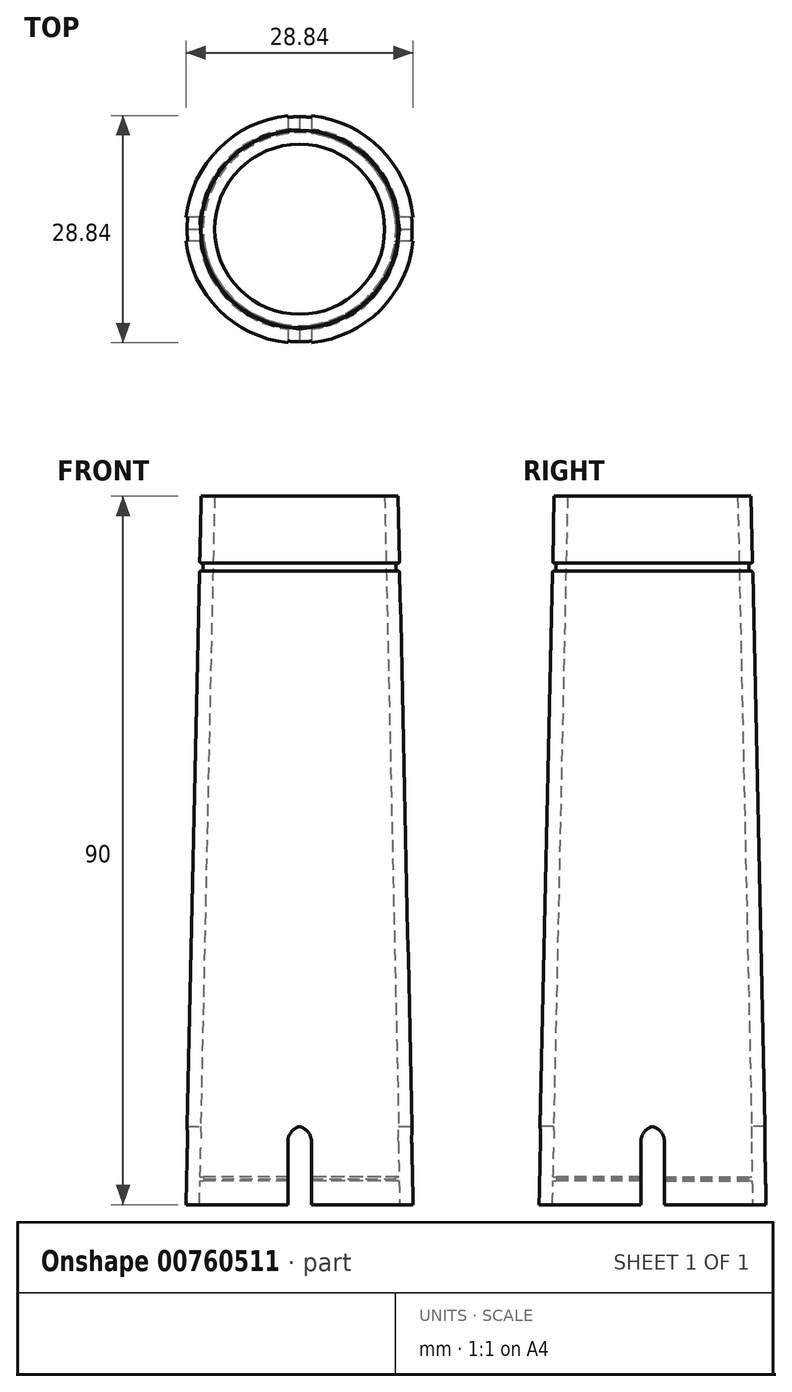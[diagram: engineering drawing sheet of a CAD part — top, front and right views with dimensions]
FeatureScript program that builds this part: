
annotation { "Feature Type Name" : "Feature", "Feature Type Description" : "" }
export const myFeature = defineFeature(function(context is Context, id is Id, definition is map)
    precondition{}
    {
        {
            var Q0;
            Q0=qCreatedBy(makeId("Top.planeOp"),FACE);
            var sketch = newSketch(context, id + "F0", { "sketchPlane" : qUnion([Q0])});
            skCircle(sketch, "E0", {"center": v(0, 0) * mm, "radius": 14.5 * mm});
            skCircle(sketch, "E1", {"center": v(0, 0) * mm, "radius": 12.8 * mm, "construction": true});
            skLineSegment(sketch, "E2", {"start": v(0, 14.5) * mm, "end": v(0, -14.5) * mm, "construction": true});
            skLineSegment(sketch, "E3", {"start": v(-14.5, 0) * mm, "end": v(14.5, 0) * mm, "construction": true});
            skSolve(sketch);
        }
        {
            var Q0;
            Q0=qCreatedBy(makeId("Top.planeOp"),FACE);
            cPlane(context, id + "F1", {"entities" : qUnion([Q0]), "cplaneType" : CPlaneType.OFFSET, "offset" : 90 * mm, "width" : 150 * mm, "height" : 150 * mm});
        }
        {
            var Q0;
            Q0=qCreatedBy(id+"F1.planeOp",FACE);
            var sketch = newSketch(context, id + "F2", { "sketchPlane" : qUnion([Q0])});
            skCircle(sketch, "E4", {"center": v(0, 0) * mm, "radius": 12.5 * mm});
            skCircle(sketch, "E5", {"center": v(0, 0) * mm, "radius": 10.8 * mm, "construction": true});
            skSolve(sketch);
        }
        {
            var Q0;
            Q0=makeQuery(id+"F0.imprint","IMPRINT",FACE,{"disambiguationData":[TD([[makeQuery(id+"F0.imprint","IMPRINT",EDGE,{"derivedFrom":sQuery(id+"F0.wireOp",EDGE,"E0")}),1.0]])]});
            var Q1;
            Q1=makeQuery(id+"F2.imprint","IMPRINT",FACE,{"disambiguationData":[TD([[makeQuery(id+"F2.imprint","IMPRINT",EDGE,{"derivedFrom":sQuery(id+"F2.wireOp",EDGE,"E4")}),1.0]])]});
            var Q2;
            Q2=sQuery(id+"F2.wireOp",EDGE,"E4");
            var Q3;
            Q3=sQuery(id+"F0.wireOp",EDGE,"E0");
            loft(context, id + "F3", {"sheetProfilesArray" : [{ "sheetProfileEntities" : qUnion([Q0]) }, { "sheetProfileEntities" : qUnion([Q1]) }], "wireProfilesArray" : [{ "wireProfileEntities" : qUnion([Q2]) }, { "wireProfileEntities" : qUnion([Q3]) }]});
        }
        {
            var Q0;
            Q0=qCreatedBy(makeId("Top.planeOp"),FACE);
            var sketch = newSketch(context, id + "F4", { "sketchPlane" : qUnion([Q0])});
            skCircle(sketch, "E6", {"center": v(0, 0) * mm, "radius": 14.5 * mm, "construction": true});
            skCircle(sketch, "E7", {"center": v(0, 0) * mm, "radius": 12.8 * mm});
            skSolve(sketch);
        }
        {
            var Q0;
            Q0=makeQuery(id+"F2.imprint","IMPRINT",FACE,{"disambiguationData":[TD([[makeQuery(id+"F2.imprint","IMPRINT",EDGE,{"derivedFrom":sQuery(id+"F2.wireOp",EDGE,"E4")}),1.0]])]});
            var sketch = newSketch(context, id + "F5", { "sketchPlane" : qUnion([Q0])});
            skCircle(sketch, "E8", {"center": v(0, 0) * mm, "radius": 10.8 * mm});
            skSolve(sketch);
        }
        {
            var Q1;
            Q1=makeQuery(id+"F5.imprint","IMPRINT",FACE,{"disambiguationData":[TD([[makeQuery(id+"F5.imprint","IMPRINT",EDGE,{"derivedFrom":sQuery(id+"F5.wireOp",EDGE,"E8")}),1.0]])]});
            var Q2;
            Q2=makeQuery(id+"F4.imprint","IMPRINT",FACE,{"disambiguationData":[TD([[makeQuery(id+"F4.imprint","IMPRINT",EDGE,{"derivedFrom":sQuery(id+"F4.wireOp",EDGE,"E7")}),1.0]])]});
            loft(context, id + "F6", {"operationType" : NewBodyOperationType.REMOVE, "sheetProfilesArray" : [{ "sheetProfileEntities" : qUnion([Q1]) }, { "sheetProfileEntities" : qUnion([Q2]) }]});
        }
        {
            var Q0;
            Q0=qCreatedBy(makeId("Top.planeOp"),FACE);
            cPlane(context, id + "F7", {"entities" : qUnion([Q0]), "cplaneType" : CPlaneType.OFFSET, "offset" : 81 * mm, "width" : 150 * mm, "height" : 150 * mm});
        }
        {
            var Q0;
            Q0=qCreatedBy(id+"F7.planeOp",FACE);
            var sketch = newSketch(context, id + "F8", { "sketchPlane" : qUnion([Q0])});
            skCircle(sketch, "E9", {"center": v(0, 0) * mm, "radius": 12.25 * mm});
            skCircle(sketch, "E10", {"center": v(0, 0) * mm, "radius": 14.5 * mm});
            skSolve(sketch);
        }
        {
            var Q0;
            Q0=makeQuery(id+"F8.imprint","IMPRINT",FACE,{"disambiguationData":[TD([[makeQuery(id+"F8.imprint","IMPRINT",EDGE,{"derivedFrom":sQuery(id+"F8.wireOp",EDGE,"E9")}),-1.0]])]});
            extrude(context, id + "F9", {"entities" : qUnion([Q0]), "operationType" : NewBodyOperationType.REMOVE, "depth" : 0.5 * mm, "offsetDistance" : 25 * mm});
        }
        {
            var Q0;
            Q0 = qSketchRegion(id + "F8", true);
            extrude(context, id + "F10", {"entities" : qUnion([Q0]), "operationType" : NewBodyOperationType.REMOVE, "oppositeDirection" : true, "depth" : 0.5 * mm, "offsetDistance" : 25 * mm});
        }
        {
            var Q0;
            Q0=makeQuery(id+"F9.boolean.opBoolean","INTERSECT",EDGE,{"derivedFrom":[makeQuery(id+"F3.opLoft","SWEPT_FACE",FACE,{"disambiguationData":[OSD([sQuery(id+"F0.wireOp",EDGE,"E0"),sQuery(id+"F2.wireOp",EDGE,"E4")])]}),makeQuery(id+"F9.opExtrude","CAP_FACE",FACE,{"disambiguationData":[OSD([sQuery(id+"F8.wireOp",EDGE,"E9"),sQuery(id+"F8.wireOp",EDGE,"E10")])],"isStart":false})]});
            var Q1;
            {var subQ0=sQuery(id+"F8.wireOp",EDGE,"E10");var subQ1=sQuery(id+"F8.wireOp",EDGE,"E9");var subQ2=sQuery(id+"F0.wireOp",EDGE,"E0");Q1=makeQuery(id+"F10.boolean.opBoolean","INTERSECT",EDGE,{"derivedFrom":[makeQuery(id+"F9.boolean.opBoolean","SPLIT",FACE,{"disambiguationData":[TD([makeQuery(id+"F3.opLoft","CAP_FACE",FACE,{"disambiguationData":[OSD([makeQuery(id+"F0.imprint","IMPRINT",FACE,{"disambiguationData":[TD([[makeQuery(id+"F0.imprint","IMPRINT",EDGE,{"derivedFrom":subQ2}),1.0]])]})])],"isStart":true})])],"derivedFrom":makeQuery(id+"F3.opLoft","SWEPT_FACE",FACE,{"disambiguationData":[OSD([subQ2,sQuery(id+"F2.wireOp",EDGE,"E4")])]})}),makeQuery(id+"F10.opExtrude","CAP_FACE",FACE,{"disambiguationData":[OSD([subQ1,subQ0])],"isStart":false})]});}
            fillet(context, id + "F11", {"entities" : qUnion([Q0, Q1]), "radius" : 0.2 * mm, "tangentPropagation" : true, "allowEdgeOverflow" : false});
        }
        {
            var Q0;
            Q0=qCreatedBy(makeId("Top.planeOp"),FACE);
            cPlane(context, id + "F12", {"entities" : qUnion([Q0]), "cplaneType" : CPlaneType.OFFSET, "offset" : 3 * mm, "width" : 150 * mm, "height" : 150 * mm});
        }
        {
            var Q0;
            Q0=qCreatedBy(id+"F12.planeOp",FACE);
            var sketch = newSketch(context, id + "F13", { "sketchPlane" : qUnion([Q0])});
            skCircle(sketch, "E11", {"center": v(0, 0) * mm, "radius": 14 * mm});
            skCircle(sketch, "E12", {"center": v(0, 0) * mm, "radius": 12.2 * mm});
            skSolve(sketch);
        }
        {
            var Q0;
            Q0 = qSketchRegion(id + "F13", true);
            extrude(context, id + "F14", {"entities" : qUnion([Q0]), "operationType" : NewBodyOperationType.ADD, "depth" : 0.5 * mm, "offsetDistance" : 25 * mm});
        }
        {
            var Q0;
            Q0 = qSketchRegion(id + "F13", true);
            extrude(context, id + "F15", {"entities" : qUnion([Q0]), "operationType" : NewBodyOperationType.ADD, "depth" : 0.5 * mm, "offsetDistance" : 25 * mm});
        }
        {
            var Q0;
            Q0=makeQuery(id+"F0.imprint","IMPRINT",FACE,{"disambiguationData":[TD([[makeQuery(id+"F0.imprint","IMPRINT",EDGE,{"derivedFrom":sQuery(id+"F0.wireOp",EDGE,"E0")}),1.0]])]});
            var sketch = newSketch(context, id + "F16", { "sketchPlane" : qUnion([Q0])});
            skLineSegment(sketch, "E13.bottom", {"start": v(-1.5, 16.5) * mm, "end": v(1.5, 16.5) * mm});
            skLineSegment(sketch, "E13.top", {"start": v(-1.5, -16.5) * mm, "end": v(1.5, -16.5) * mm});
            skLineSegment(sketch, "E13.left", {"start": v(-1.5, 16.5) * mm, "end": v(-1.5, -16.5) * mm});
            skLineSegment(sketch, "E13.right", {"start": v(1.5, 16.5) * mm, "end": v(1.5, -16.5) * mm});
            skPoint(sketch, "E13.middle", {"position": v(0, 0) * mm});
            skLineSegment(sketch, "E14.bottom", {"start": v(16.5, 1.5) * mm, "end": v(-16.5, 1.5) * mm});
            skLineSegment(sketch, "E14.top", {"start": v(16.5, -1.5) * mm, "end": v(-16.5, -1.5) * mm});
            skLineSegment(sketch, "E14.left", {"start": v(16.5, 1.5) * mm, "end": v(16.5, -1.5) * mm});
            skLineSegment(sketch, "E14.right", {"start": v(-16.5, 1.5) * mm, "end": v(-16.5, -1.5) * mm});
            skSolve(sketch);
        }
        {
            var Q0;
            Q0 = qSketchRegion(id + "F16", true);
            extrude(context, id + "F17", {"entities" : qUnion([Q0]), "operationType" : NewBodyOperationType.REMOVE, "depth" : 10 * mm, "offsetDistance" : 25 * mm});
        }
        {
            var Q0;
            {var subQ0=sQuery(id+"F13.wireOp",EDGE,"E12");var subQ1=sQuery(id+"F16.wireOp",EDGE,"E13.left");var subQ4=sQuery(id+"F16.wireOp",EDGE,"E14.top");var subQ5=makeQuery(id+"F16.imprint","INTERSECT",VERTEX,{"derivedFrom":[subQ1,subQ4]});Q0=makeQuery(id+"F17.boolean.opBoolean","SPLIT",EDGE,{"disambiguationData":[TD([makeQuery(id+"F17.opExtrude","SWEPT_FACE",FACE,{"disambiguationData":[OSD([subQ1]),TDD([makeQuery(id+"F16.imprint","IMPRINT",EDGE,{"disambiguationData":[TD([[subQ5,-1.0]])],"derivedFrom":subQ1}),makeQuery(id+"F16.imprint","IMPRINT",EDGE,{"disambiguationData":[TD([[makeQuery(id+"F16.imprint","INTERSECT",VERTEX,{"derivedFrom":[sQuery(id+"F16.wireOp",EDGE,"E13.top"),subQ1]}),1.0]])],"derivedFrom":subQ1})])]})])],"derivedFrom":makeQuery(id+"F14.opExtrude","CAP_EDGE",EDGE,{"disambiguationData":[OSD([subQ0])],"isStart":true})});}
            var Q1;
            {var subQ0=sQuery(id+"F13.wireOp",EDGE,"E12");var subQ1=sQuery(id+"F16.wireOp",EDGE,"E13.left");var subQ4=sQuery(id+"F16.wireOp",EDGE,"E14.top");var subQ5=makeQuery(id+"F16.imprint","INTERSECT",VERTEX,{"derivedFrom":[subQ1,subQ4]});Q1=makeQuery(id+"F17.boolean.opBoolean","SPLIT",EDGE,{"disambiguationData":[TD([makeQuery(id+"F17.opExtrude","SWEPT_FACE",FACE,{"disambiguationData":[OSD([subQ1]),TDD([makeQuery(id+"F16.imprint","IMPRINT",EDGE,{"disambiguationData":[TD([[subQ5,-1.0]])],"derivedFrom":subQ1}),makeQuery(id+"F16.imprint","IMPRINT",EDGE,{"disambiguationData":[TD([[makeQuery(id+"F16.imprint","INTERSECT",VERTEX,{"derivedFrom":[sQuery(id+"F16.wireOp",EDGE,"E13.top"),subQ1]}),1.0]])],"derivedFrom":subQ1})])]})])],"derivedFrom":makeQuery(id+"F14.opExtrude","CAP_EDGE",EDGE,{"disambiguationData":[OSD([subQ0])],"isStart":false})});}
            var Q2;
            {var subQ0=sQuery(id+"F13.wireOp",EDGE,"E12");var subQ1=sQuery(id+"F16.wireOp",EDGE,"E14.top");var subQ2=sQuery(id+"F16.wireOp",EDGE,"E13.right");var subQ3=makeQuery(id+"F16.imprint","INTERSECT",VERTEX,{"derivedFrom":[subQ2,subQ1]});Q2=makeQuery(id+"F17.boolean.opBoolean","SPLIT",EDGE,{"disambiguationData":[TD([makeQuery(id+"F17.opExtrude","SWEPT_FACE",FACE,{"disambiguationData":[OSD([subQ2]),TDD([makeQuery(id+"F16.imprint","IMPRINT",EDGE,{"disambiguationData":[TD([[subQ3,-1.0]])],"derivedFrom":subQ2}),makeQuery(id+"F16.imprint","IMPRINT",EDGE,{"disambiguationData":[TD([[makeQuery(id+"F16.imprint","INTERSECT",VERTEX,{"derivedFrom":[sQuery(id+"F16.wireOp",EDGE,"E13.top"),subQ2]}),1.0]])],"derivedFrom":subQ2})])]})])],"derivedFrom":makeQuery(id+"F14.opExtrude","CAP_EDGE",EDGE,{"disambiguationData":[OSD([subQ0])],"isStart":true})});}
            var Q3;
            {var subQ0=sQuery(id+"F13.wireOp",EDGE,"E12");var subQ1=sQuery(id+"F16.wireOp",EDGE,"E14.top");var subQ2=sQuery(id+"F16.wireOp",EDGE,"E13.right");var subQ3=makeQuery(id+"F16.imprint","INTERSECT",VERTEX,{"derivedFrom":[subQ2,subQ1]});Q3=makeQuery(id+"F17.boolean.opBoolean","SPLIT",EDGE,{"disambiguationData":[TD([makeQuery(id+"F17.opExtrude","SWEPT_FACE",FACE,{"disambiguationData":[OSD([subQ2]),TDD([makeQuery(id+"F16.imprint","IMPRINT",EDGE,{"disambiguationData":[TD([[subQ3,-1.0]])],"derivedFrom":subQ2}),makeQuery(id+"F16.imprint","IMPRINT",EDGE,{"disambiguationData":[TD([[makeQuery(id+"F16.imprint","INTERSECT",VERTEX,{"derivedFrom":[sQuery(id+"F16.wireOp",EDGE,"E13.top"),subQ2]}),1.0]])],"derivedFrom":subQ2})])]})])],"derivedFrom":makeQuery(id+"F14.opExtrude","CAP_EDGE",EDGE,{"disambiguationData":[OSD([subQ0])],"isStart":false})});}
            var Q4;
            {var subQ0=sQuery(id+"F13.wireOp",EDGE,"E12");var subQ1=sQuery(id+"F16.wireOp",EDGE,"E14.bottom");var subQ2=sQuery(id+"F16.wireOp",EDGE,"E13.right");var subQ3=makeQuery(id+"F16.imprint","INTERSECT",VERTEX,{"derivedFrom":[subQ2,subQ1]});Q4=makeQuery(id+"F17.boolean.opBoolean","SPLIT",EDGE,{"disambiguationData":[TD([makeQuery(id+"F17.opExtrude","SWEPT_FACE",FACE,{"disambiguationData":[OSD([subQ2]),TDD([makeQuery(id+"F16.imprint","IMPRINT",EDGE,{"disambiguationData":[TD([[makeQuery(id+"F16.imprint","INTERSECT",VERTEX,{"derivedFrom":[sQuery(id+"F16.wireOp",EDGE,"E13.bottom"),subQ2]}),-1.0]])],"derivedFrom":subQ2}),makeQuery(id+"F16.imprint","IMPRINT",EDGE,{"disambiguationData":[TD([[subQ3,1.0]])],"derivedFrom":subQ2})])]})])],"derivedFrom":makeQuery(id+"F14.opExtrude","CAP_EDGE",EDGE,{"disambiguationData":[OSD([subQ0])],"isStart":true})});}
            var Q5;
            {var subQ0=sQuery(id+"F13.wireOp",EDGE,"E12");var subQ1=sQuery(id+"F16.wireOp",EDGE,"E14.bottom");var subQ2=sQuery(id+"F16.wireOp",EDGE,"E13.right");var subQ3=makeQuery(id+"F16.imprint","INTERSECT",VERTEX,{"derivedFrom":[subQ2,subQ1]});Q5=makeQuery(id+"F17.boolean.opBoolean","SPLIT",EDGE,{"disambiguationData":[TD([makeQuery(id+"F17.opExtrude","SWEPT_FACE",FACE,{"disambiguationData":[OSD([subQ2]),TDD([makeQuery(id+"F16.imprint","IMPRINT",EDGE,{"disambiguationData":[TD([[makeQuery(id+"F16.imprint","INTERSECT",VERTEX,{"derivedFrom":[sQuery(id+"F16.wireOp",EDGE,"E13.bottom"),subQ2]}),-1.0]])],"derivedFrom":subQ2}),makeQuery(id+"F16.imprint","IMPRINT",EDGE,{"disambiguationData":[TD([[subQ3,1.0]])],"derivedFrom":subQ2})])]})])],"derivedFrom":makeQuery(id+"F14.opExtrude","CAP_EDGE",EDGE,{"disambiguationData":[OSD([subQ0])],"isStart":false})});}
            var Q6;
            {var subQ0=sQuery(id+"F13.wireOp",EDGE,"E12");var subQ1=sQuery(id+"F16.wireOp",EDGE,"E14.bottom");var subQ2=sQuery(id+"F16.wireOp",EDGE,"E13.left");var subQ3=makeQuery(id+"F16.imprint","INTERSECT",VERTEX,{"derivedFrom":[subQ2,subQ1]});Q6=makeQuery(id+"F17.boolean.opBoolean","SPLIT",EDGE,{"disambiguationData":[TD([makeQuery(id+"F17.opExtrude","SWEPT_FACE",FACE,{"disambiguationData":[OSD([subQ2]),TDD([makeQuery(id+"F16.imprint","IMPRINT",EDGE,{"disambiguationData":[TD([[makeQuery(id+"F16.imprint","INTERSECT",VERTEX,{"derivedFrom":[sQuery(id+"F16.wireOp",EDGE,"E13.bottom"),subQ2]}),-1.0]])],"derivedFrom":subQ2}),makeQuery(id+"F16.imprint","IMPRINT",EDGE,{"disambiguationData":[TD([[subQ3,1.0]])],"derivedFrom":subQ2})])]})])],"derivedFrom":makeQuery(id+"F14.opExtrude","CAP_EDGE",EDGE,{"disambiguationData":[OSD([subQ0])],"isStart":true})});}
            var Q7;
            {var subQ0=sQuery(id+"F13.wireOp",EDGE,"E12");var subQ1=sQuery(id+"F16.wireOp",EDGE,"E14.bottom");var subQ2=sQuery(id+"F16.wireOp",EDGE,"E13.left");var subQ3=makeQuery(id+"F16.imprint","INTERSECT",VERTEX,{"derivedFrom":[subQ2,subQ1]});Q7=makeQuery(id+"F17.boolean.opBoolean","SPLIT",EDGE,{"disambiguationData":[TD([makeQuery(id+"F17.opExtrude","SWEPT_FACE",FACE,{"disambiguationData":[OSD([subQ2]),TDD([makeQuery(id+"F16.imprint","IMPRINT",EDGE,{"disambiguationData":[TD([[makeQuery(id+"F16.imprint","INTERSECT",VERTEX,{"derivedFrom":[sQuery(id+"F16.wireOp",EDGE,"E13.bottom"),subQ2]}),-1.0]])],"derivedFrom":subQ2}),makeQuery(id+"F16.imprint","IMPRINT",EDGE,{"disambiguationData":[TD([[subQ3,1.0]])],"derivedFrom":subQ2})])]})])],"derivedFrom":makeQuery(id+"F14.opExtrude","CAP_EDGE",EDGE,{"disambiguationData":[OSD([subQ0])],"isStart":false})});}
            fillet(context, id + "F18", {"entities" : qUnion([Q0, Q1, Q2, Q3, Q4, Q5, Q6, Q7]), "radius" : 0.3 * mm, "tangentPropagation" : true, "allowEdgeOverflow" : false});
        }
        {
            var Q0;
            {var subQ0=sQuery(id+"F16.wireOp",EDGE,"E14.top");Q0=makeQuery(id+"F17.boolean.opBoolean","COPY",EDGE,{"derivedFrom":makeQuery(id+"F17.opExtrude","CAP_EDGE",EDGE,{"disambiguationData":[OSD([subQ0]),TDD([makeQuery(id+"F16.imprint","IMPRINT",EDGE,{"disambiguationData":[TD([[makeQuery(id+"F16.imprint","INTERSECT",VERTEX,{"derivedFrom":[subQ0,sQuery(id+"F16.wireOp",EDGE,"E14.left")]}),-1.0]])],"derivedFrom":subQ0}),makeQuery(id+"F16.imprint","IMPRINT",EDGE,{"disambiguationData":[TD([[makeQuery(id+"F16.imprint","INTERSECT",VERTEX,{"derivedFrom":[sQuery(id+"F16.wireOp",EDGE,"E13.right"),subQ0]}),1.0]])],"derivedFrom":subQ0})])],"isStart":false})});}
            var Q1;
            {var subQ0=sQuery(id+"F16.wireOp",EDGE,"E14.bottom");Q1=makeQuery(id+"F17.boolean.opBoolean","COPY",EDGE,{"derivedFrom":makeQuery(id+"F17.opExtrude","CAP_EDGE",EDGE,{"disambiguationData":[OSD([subQ0]),TDD([makeQuery(id+"F16.imprint","IMPRINT",EDGE,{"disambiguationData":[TD([[makeQuery(id+"F16.imprint","INTERSECT",VERTEX,{"derivedFrom":[subQ0,sQuery(id+"F16.wireOp",EDGE,"E14.left")]}),-1.0]])],"derivedFrom":subQ0}),makeQuery(id+"F16.imprint","IMPRINT",EDGE,{"disambiguationData":[TD([[makeQuery(id+"F16.imprint","INTERSECT",VERTEX,{"derivedFrom":[sQuery(id+"F16.wireOp",EDGE,"E13.right"),subQ0]}),1.0]])],"derivedFrom":subQ0})])],"isStart":false})});}
            var Q2;
            {var subQ0=sQuery(id+"F16.wireOp",EDGE,"E13.left");Q2=makeQuery(id+"F17.boolean.opBoolean","COPY",EDGE,{"derivedFrom":makeQuery(id+"F17.opExtrude","CAP_EDGE",EDGE,{"disambiguationData":[OSD([subQ0]),TDD([makeQuery(id+"F16.imprint","IMPRINT",EDGE,{"disambiguationData":[TD([[makeQuery(id+"F16.imprint","INTERSECT",VERTEX,{"derivedFrom":[subQ0,sQuery(id+"F16.wireOp",EDGE,"E14.top")]}),-1.0]])],"derivedFrom":subQ0}),makeQuery(id+"F16.imprint","IMPRINT",EDGE,{"disambiguationData":[TD([[makeQuery(id+"F16.imprint","INTERSECT",VERTEX,{"derivedFrom":[sQuery(id+"F16.wireOp",EDGE,"E13.top"),subQ0]}),1.0]])],"derivedFrom":subQ0})])],"isStart":false})});}
            var Q3;
            {var subQ0=sQuery(id+"F16.wireOp",EDGE,"E13.right");Q3=makeQuery(id+"F17.boolean.opBoolean","COPY",EDGE,{"derivedFrom":makeQuery(id+"F17.opExtrude","CAP_EDGE",EDGE,{"disambiguationData":[OSD([subQ0]),TDD([makeQuery(id+"F16.imprint","IMPRINT",EDGE,{"disambiguationData":[TD([[makeQuery(id+"F16.imprint","INTERSECT",VERTEX,{"derivedFrom":[subQ0,sQuery(id+"F16.wireOp",EDGE,"E14.top")]}),-1.0]])],"derivedFrom":subQ0}),makeQuery(id+"F16.imprint","IMPRINT",EDGE,{"disambiguationData":[TD([[makeQuery(id+"F16.imprint","INTERSECT",VERTEX,{"derivedFrom":[sQuery(id+"F16.wireOp",EDGE,"E13.top"),subQ0]}),1.0]])],"derivedFrom":subQ0})])],"isStart":false})});}
            var Q4;
            {var subQ0=sQuery(id+"F16.wireOp",EDGE,"E14.top");Q4=makeQuery(id+"F17.boolean.opBoolean","COPY",EDGE,{"derivedFrom":makeQuery(id+"F17.opExtrude","CAP_EDGE",EDGE,{"disambiguationData":[OSD([subQ0]),TDD([makeQuery(id+"F16.imprint","IMPRINT",EDGE,{"disambiguationData":[TD([[makeQuery(id+"F16.imprint","INTERSECT",VERTEX,{"derivedFrom":[sQuery(id+"F16.wireOp",EDGE,"E13.left"),subQ0]}),-1.0]])],"derivedFrom":subQ0}),makeQuery(id+"F16.imprint","IMPRINT",EDGE,{"disambiguationData":[TD([[makeQuery(id+"F16.imprint","INTERSECT",VERTEX,{"derivedFrom":[subQ0,sQuery(id+"F16.wireOp",EDGE,"E14.right")]}),1.0]])],"derivedFrom":subQ0})])],"isStart":false})});}
            var Q5;
            {var subQ0=sQuery(id+"F16.wireOp",EDGE,"E14.bottom");Q5=makeQuery(id+"F17.boolean.opBoolean","COPY",EDGE,{"derivedFrom":makeQuery(id+"F17.opExtrude","CAP_EDGE",EDGE,{"disambiguationData":[OSD([subQ0]),TDD([makeQuery(id+"F16.imprint","IMPRINT",EDGE,{"disambiguationData":[TD([[makeQuery(id+"F16.imprint","INTERSECT",VERTEX,{"derivedFrom":[sQuery(id+"F16.wireOp",EDGE,"E13.left"),subQ0]}),-1.0]])],"derivedFrom":subQ0}),makeQuery(id+"F16.imprint","IMPRINT",EDGE,{"disambiguationData":[TD([[makeQuery(id+"F16.imprint","INTERSECT",VERTEX,{"derivedFrom":[subQ0,sQuery(id+"F16.wireOp",EDGE,"E14.right")]}),1.0]])],"derivedFrom":subQ0})])],"isStart":false})});}
            var Q6;
            {var subQ0=sQuery(id+"F16.wireOp",EDGE,"E13.left");Q6=makeQuery(id+"F17.boolean.opBoolean","COPY",EDGE,{"derivedFrom":makeQuery(id+"F17.opExtrude","CAP_EDGE",EDGE,{"disambiguationData":[OSD([subQ0]),TDD([makeQuery(id+"F16.imprint","IMPRINT",EDGE,{"disambiguationData":[TD([[makeQuery(id+"F16.imprint","INTERSECT",VERTEX,{"derivedFrom":[sQuery(id+"F16.wireOp",EDGE,"E13.bottom"),subQ0]}),-1.0]])],"derivedFrom":subQ0}),makeQuery(id+"F16.imprint","IMPRINT",EDGE,{"disambiguationData":[TD([[makeQuery(id+"F16.imprint","INTERSECT",VERTEX,{"derivedFrom":[subQ0,sQuery(id+"F16.wireOp",EDGE,"E14.bottom")]}),1.0]])],"derivedFrom":subQ0})])],"isStart":false})});}
            var Q7;
            {var subQ0=sQuery(id+"F16.wireOp",EDGE,"E13.right");Q7=makeQuery(id+"F17.boolean.opBoolean","COPY",EDGE,{"derivedFrom":makeQuery(id+"F17.opExtrude","CAP_EDGE",EDGE,{"disambiguationData":[OSD([subQ0]),TDD([makeQuery(id+"F16.imprint","IMPRINT",EDGE,{"disambiguationData":[TD([[makeQuery(id+"F16.imprint","INTERSECT",VERTEX,{"derivedFrom":[sQuery(id+"F16.wireOp",EDGE,"E13.bottom"),subQ0]}),-1.0]])],"derivedFrom":subQ0}),makeQuery(id+"F16.imprint","IMPRINT",EDGE,{"disambiguationData":[TD([[makeQuery(id+"F16.imprint","INTERSECT",VERTEX,{"derivedFrom":[subQ0,sQuery(id+"F16.wireOp",EDGE,"E14.bottom")]}),1.0]])],"derivedFrom":subQ0})])],"isStart":false})});}
            fillet(context, id + "F19", {"entities" : qUnion([Q0, Q1, Q2, Q3, Q4, Q5, Q6, Q7]), "radius" : 2 * mm, "tangentPropagation" : true, "allowEdgeOverflow" : false});
        }
    });
